# Revit family: Basin-Wall_Hung-American_Standard-Decorum-9024_Series
name_source: partatom
category: Plumbing Fixtures
revit_build: Autodesk Revit 2014 (Build: 20130308_1515(x64)
units: mm (PartAtom-declared; Revit-internal decimal feet)

## types (15) — shared parameters
ADA Compliant = Yes
Assembly Code = D2010310
Basin Shape = Rectangular
CW Connection = Yes
CWFU = 1.5
Cold Water Connection Radius = 3/16"
Default Elevation = 34"
HW Connection = Yes
HWFU = 1.5
Height = 7 3/8"
Hot Water Connection Radius = 3/16"
Installation Type = Wall-Hung
Length = 18 1/4"
Manufacturer = American Standard
Material = Vitreous China-American Standard-020-White
Price = Prices may vary. Please consult Manufacturer Representative for most up-to-date price list.
Product Documentation Link = http://www.americanstandard-us.com
Product Page URL = http://www.americanstandard-us.com
URL = http://www.americanstandard-us.com
Vent Connection = No
WFU = 2
Waste Connection = Yes
Waste Connection Radius = 5/8"
Width = 20"

## per-type parameters (varying)
| type | Center H | Center Hole | Description | Left Center Hole | Left Hand Soap | Left Hand Soap Dispenser | Left and Right Centers | Overflow | Right Center Hole | Right Hand Soap | Right Hand Soap Dispenser | Visible |
| 9024.000EC | No | 20" | Decorum® Wall-Hung Lavatory With Everclean® No faucet holes. | 15" | No | 20" | No | 0" | 15" | No | 20" | Yes |
| 9024.001EC | Yes | 2 1/4" | Decorum® Wall-Hung Lavatory With Everclean® with center hole only (CHO) | 15" | No | 20" | No | 0" | 15" | No | 20" | Yes |
| 9024.021EC | Yes | 2 1/4" | Decorum® Wall-Hung Lavatory With Everclean® with CHO with left hand soap dispenser | 20" | Yes | 4 5/8" | No | 0" | 22" | No | 25" | Yes |
| 9024.011EC | Yes | 2 1/4" | Decorum® Wall-Hung Lavatory With Everclean® with CHO with right hand soap dispenser | 22" | No | 25" | No | 0" | 22" | Yes | 4 5/8" | Yes |
| 9024.901EC | Yes | 2 1/4" | Decorum® Wall-Hung Lavatory With Everclean® with CHO Less Overflow | 20" | No | 25" | No | 15" | 20" | No | 22" | No |
| 9024.921EC | Yes | 2 1/4" | Decorum® Wall-Hung Lavatory With Everclean® with left hand soap dispenser less overflow | 22" | Yes | 4 5/8" | No | 15" | 22" | No | 20" | No |
| 9024.911EC | Yes | 2 1/4" | Decorum® Wall-Hung Lavatory With Everclean® with right hand soap dispenser less overflow | 22" | No | 25" | No | 15" | 22" | Yes | 4 5/8" | No |
| 9024.004EC | Yes | 2 1/4" | Decorum® Wall-Hung Lavatory With Everclean® 4" Centers | 2" | No | 20" | Yes | 0" | 2" | No | 20" | Yes |
| 9024.024EC | Yes | 2 1/4" | Decorum® Wall-Hung Lavatory With Everclean® 4" centers with left hand soap dispenser | 2" | Yes | 4 5/8" | Yes | 0" | 2" | No | 20" | Yes |
| 9024.014EC | Yes | 2 1/4" | Decorum® Wall-Hung Lavatory With Everclean® 4" centers with right hand soap dispenser | 2" | No | 20" | Yes | 0" | 2" | Yes | 4 5/8" | Yes |
| 9024.904EC | Yes | 2 1/4" | Decorum® Wall-Hung Lavatory With Everclean® 4" centers less overflow | 2" | No | 20" | Yes | 15" | 2" | No | 20" | No |
| 9024.924EC | Yes | 2 1/4" | Decorum® Wall-Hung Lavatory With Everclean® 4" centers with left hand soap dispenser less overflow | 2" | Yes | 4 5/8" | Yes | 15" | 2" | Yes | 4 5/8" | No |
| 9024.914EC | Yes | 2 1/4" | Decorum® Wall-Hung Lavatory With Everclean® 4" centers with right hand soap dispenser less overflow | 2" | No | 22" | Yes | 15" | 2" | Yes | 4 5/8" | No |
| 9024.008EC | Yes | 2 1/4" | Decorum® Wall-Hung Lavatory With Everclean® 8" centers | 4" | No | 20" | Yes | 0" | 4" | No | 20" | Yes |
| 9024.908EC | Yes | 2 1/4" | Decorum® Wall-Hung Lavatory With Everclean® 8" centers less overflow | 4" | No | 20" | Yes | 15" | 4" | No | 20" | No |

note: column(s) folded — value = type name in every type: Model

## geometry (parser evidence)
native form markers: Blend x20, Sweep x1
no freeform markers — native parametric forms only
